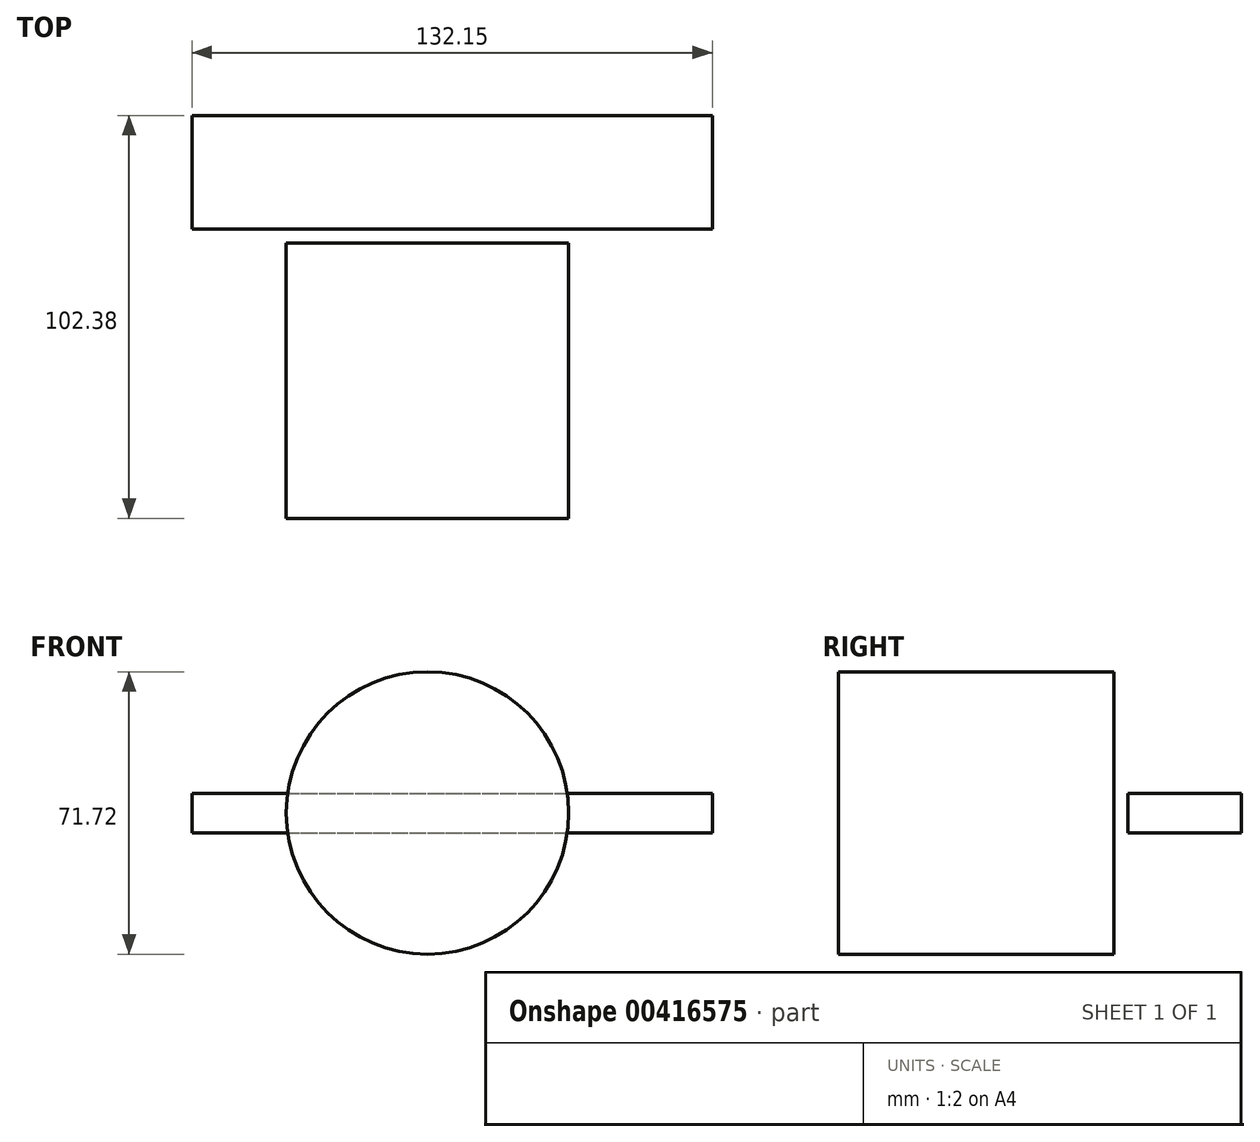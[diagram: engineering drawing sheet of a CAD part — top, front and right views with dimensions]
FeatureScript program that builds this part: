
annotation { "Feature Type Name" : "Feature", "Feature Type Description" : "" }
export const myFeature = defineFeature(function(context is Context, id is Id, definition is map)
    precondition{}
    {
        {
            var Q0;
            Q0=qCreatedBy(makeId("Front.planeOp"),FACE);
            var sketch = newSketch(context, id + "F0", { "sketchPlane" : qUnion([Q0])});
            skLineSegment(sketch, "E0.bottom", {"start": v(-64.48, 28.67) * mm, "end": v(64.48, 28.67) * mm});
            skLineSegment(sketch, "E0.top", {"start": v(-64.48, -28.67) * mm, "end": v(64.48, -28.67) * mm});
            skLineSegment(sketch, "E0.left", {"start": v(-64.48, 28.67) * mm, "end": v(-64.48, -28.67) * mm});
            skLineSegment(sketch, "E0.right", {"start": v(64.48, 28.67) * mm, "end": v(64.48, -28.67) * mm});
            skPoint(sketch, "E0.middle", {"position": v(0, 0) * mm});
            skCircle(sketch, "E1", {"center": v(0, 0) * mm, "radius": 35.86 * mm});
            skSolve(sketch);
        }
        {
            var Q0;
            {var subQ0=sQuery(id+"F0.wireOp",EDGE,"E1");var subQ1=sQuery(id+"F0.wireOp",EDGE,"E0.bottom");var subQ2=makeQuery(id+"F0.imprint","INTERSECT",VERTEX,{"disambiguationData":[OD(0.0)],"derivedFrom":[subQ1,subQ0]});Q0=makeQuery(id+"F0.imprint","IMPRINT",FACE,{"disambiguationData":[TD([[makeQuery(id+"F0.imprint","IMPRINT",EDGE,{"disambiguationData":[TD([[subQ2,-1.0]])],"derivedFrom":subQ1}),1.0]])]});}
            var Q1;
            {var subQ0=sQuery(id+"F0.wireOp",EDGE,"E1");var subQ1=sQuery(id+"F0.wireOp",EDGE,"E0.bottom");var subQ2=makeQuery(id+"F0.imprint","INTERSECT",VERTEX,{"disambiguationData":[OD(0.0)],"derivedFrom":[subQ1,subQ0]});Q1=makeQuery(id+"F0.imprint","IMPRINT",FACE,{"disambiguationData":[TD([[makeQuery(id+"F0.imprint","IMPRINT",EDGE,{"disambiguationData":[TD([[subQ2,-1.0]])],"derivedFrom":subQ1}),-1.0]])]});}
            var Q2;
            {var subQ0=sQuery(id+"F0.wireOp",EDGE,"E1");var subQ1=sQuery(id+"F0.wireOp",EDGE,"E0.top");var subQ2=makeQuery(id+"F0.imprint","INTERSECT",VERTEX,{"disambiguationData":[OD(0.0)],"derivedFrom":[subQ1,subQ0]});Q2=makeQuery(id+"F0.imprint","IMPRINT",FACE,{"disambiguationData":[TD([[makeQuery(id+"F0.imprint","IMPRINT",EDGE,{"disambiguationData":[TD([[subQ2,-1.0]])],"derivedFrom":subQ1}),-1.0]])]});}
            extrude(context, id + "F1", {"entities" : qUnion([Q0, Q1, Q2]), "endBound" : BoundingType.SYMMETRIC, "depth" : 70 * mm});
        }
        {
            var Q0;
            Q0=qCreatedBy(makeId("Top.planeOp"),FACE);
            var sketch = newSketch(context, id + "F2", { "sketchPlane" : qUnion([Q0])});
            skLineSegment(sketch, "E2.bottom", {"start": v(-59.78, 38.55) * mm, "end": v(72.37, 38.55) * mm});
            skLineSegment(sketch, "E2.top", {"start": v(-59.78, 67.38) * mm, "end": v(72.37, 67.38) * mm});
            skLineSegment(sketch, "E2.left", {"start": v(-59.78, 38.55) * mm, "end": v(-59.78, 67.38) * mm});
            skLineSegment(sketch, "E2.right", {"start": v(72.37, 38.55) * mm, "end": v(72.37, 67.38) * mm});
            skSolve(sketch);
        }
        {
            var Q0;
            Q0=makeQuery(id+"F2.imprint","IMPRINT",FACE,{"disambiguationData":[TD([[makeQuery(id+"F2.imprint","IMPRINT",EDGE,{"derivedFrom":sQuery(id+"F2.wireOp",EDGE,"E2.bottom")}),1.0]])]});
            extrude(context, id + "F3", {"entities" : qUnion([Q0]), "endBound" : BoundingType.SYMMETRIC, "depth" : 10 * mm});
        }
    });
